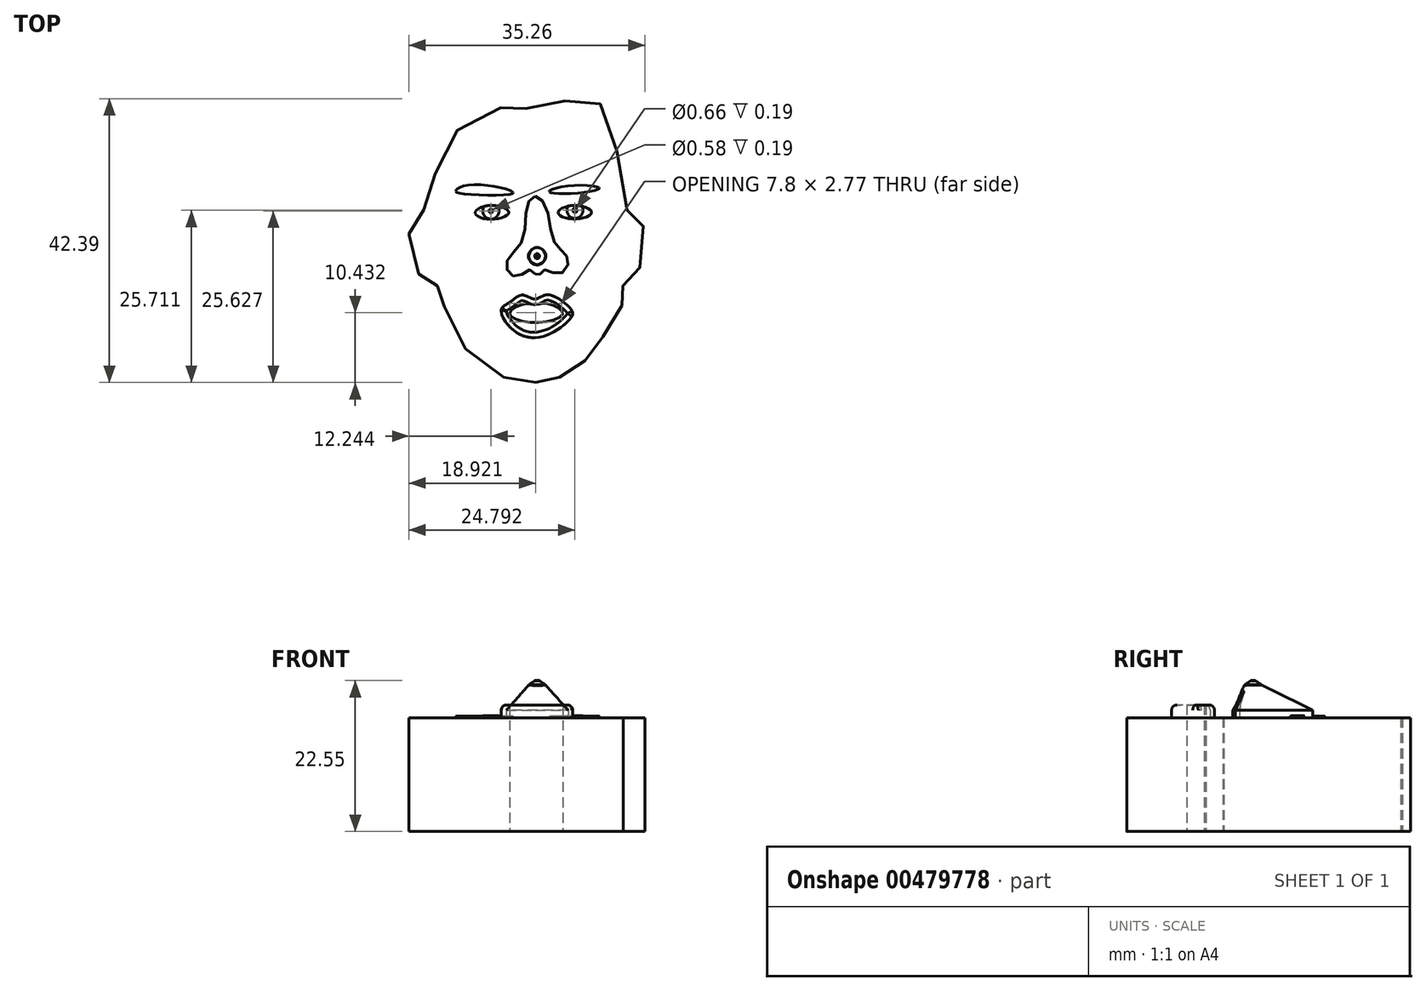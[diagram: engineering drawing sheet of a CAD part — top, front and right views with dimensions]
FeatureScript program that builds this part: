
annotation { "Feature Type Name" : "Feature", "Feature Type Description" : "" }
export const myFeature = defineFeature(function(context is Context, id is Id, definition is map)
    precondition{}
    {
        {
            var Q0;
            Q0=qCreatedBy(makeId("Top.planeOp"),FACE);
            var sketch = newSketch(context, id + "F0", { "sketchPlane" : qUnion([Q0])});
            skFitSpline(sketch, "E0", {"points": [v(0.4, -22.75) * mm, v(-4.87, -21.75) * mm, v(-12.74, -13.42) * mm, v(-13.89, -8.3) * mm, v(-14.73, -8.38) * mm, v(-17.1, -6.47) * mm, v(-18.24, 0.86) * mm, v(-15.72, 3.84) * mm, v(-12.97, 13.09) * mm, v(-3.8, 18.44) * mm, v(-1.2, 18.14) * mm, v(6.52, 19.59) * mm, v(11.26, 17.14) * mm, v(14.54, 1.94) * mm, v(16.3, 0.95) * mm, v(15.46, -6.54) * mm, v(13.47, -8.22) * mm, v(13.43, -8.87) * mm, v(13.1, -11.77) * mm, v(9.22, -17.47) * mm, v(7.15, -20.1) * mm, v(2.92, -22.33) * mm, v(0.4, -22.75) * mm]});
            skFitSpline(sketch, "E1", {"points": [v(-11.56, 5.85) * mm, v(-10.22, 6.65) * mm, v(-4.5, 6.26) * mm, v(-3, 5.51) * mm, v(-10, 5.38) * mm, v(-11.56, 5.85) * mm]});
            skFitSpline(sketch, "E2", {"points": [v(2.41, 5.72) * mm, v(5.43, 6.65) * mm, v(9.9, 6.3) * mm, v(6.97, 5.59) * mm, v(2.41, 5.72) * mm]});
            skFitSpline(sketch, "E3", {"points": [v(3.74, 2.65) * mm, v(6, 1.68) * mm, v(8.72, 2.63) * mm, v(6.32, 3.72) * mm, v(3.74, 2.65) * mm]});
            skCircle(sketch, "E4", {"center": v(6.25, 2.96) * mm, "radius": 0.33 * mm});
            skArc(sketch, "E5", {"start": v(5.24, 3.6) * mm, "mid": v(6.25, 1.76) * mm, "end": v(7.27, 3.6) * mm});
            skFitSpline(sketch, "E6", {"points": [v(-8.65, 2.59) * mm, v(-6.37, 3.7) * mm, v(-3.61, 2.65) * mm, v(-6.23, 1.61) * mm, v(-8.65, 2.59) * mm]});
            skCircle(sketch, "E7", {"center": v(-6.3, 2.88) * mm, "radius": 0.3 * mm});
            skArc(sketch, "E8", {"start": v(-7.3, 3.56) * mm, "mid": v(-6.26, 1.66) * mm, "end": v(-5.33, 3.62) * mm});
            skFitSpline(sketch, "E9", {"points": [v(-4.77, -11.97) * mm, v(-3.44, -10.74) * mm, v(-1.6, -9.67) * mm, v(0.29, -10.29) * mm, v(2.2, -9.64) * mm, v(5.8, -12.04) * mm, v(5.69, -13.03) * mm, v(3.08, -15.2) * mm, v(-1.88, -15.61) * mm, v(-4.77, -11.97) * mm]});
            skFitSpline(sketch, "E10", {"points": [v(-3.52, -12.43) * mm, v(-1.17, -11) * mm, v(0.27, -11.15) * mm, v(1.78, -10.9) * mm, v(4.43, -12.34) * mm, v(0.56, -13.8) * mm, v(-3.52, -12.43) * mm]});
            skFitSpline(sketch, "E11", {"points": [v(0.34, 5.06) * mm, v(1.94, 3.41) * mm, v(3.16, -1.8) * mm, v(4.65, -3.4) * mm, v(5.24, -5.08) * mm, v(3.78, -6.54) * mm, v(1.74, -5.91) * mm, v(0.98, -6.62) * mm, v(0.49, -6.67) * mm, v(-0.4, -5.91) * mm, v(-2.12, -6.85) * mm, v(-3.77, -6.2) * mm, v(-3.69, -4.22) * mm, v(-1.63, -1.63) * mm, v(-0.9, 3.56) * mm, v(0.34, 5.06) * mm]});
            skSolve(sketch);
        }
        {
            var Q0;
            Q0=makeQuery(id+"F0.imprint","IMPRINT",FACE,{"disambiguationData":[TD([[makeQuery(id+"F0.imprint","IMPRINT",EDGE,{"derivedFrom":sQuery(id+"F0.wireOp",EDGE,"E0")}),-1.0]])]});
            extrude(context, id + "F1", {"entities" : qUnion([Q0]), "depth" : 17 * mm});
        }
        {
            var Q0;
            Q0=makeQuery(id+"F0.imprint","IMPRINT",FACE,{"disambiguationData":[TD([[makeQuery(id+"F0.imprint","IMPRINT",EDGE,{"derivedFrom":sQuery(id+"F0.wireOp",EDGE,"E11")}),-1.0]])]});
            extrude(context, id + "F2", {"entities" : qUnion([Q0]), "operationType" : NewBodyOperationType.ADD, "depth" : 18.1 * mm});
        }
        {
            var Q0;
            Q0=makeQuery(id+"F0.imprint","IMPRINT",FACE,{"disambiguationData":[TD([[makeQuery(id+"F0.imprint","IMPRINT",EDGE,{"derivedFrom":sQuery(id+"F0.wireOp",EDGE,"E2")}),-1.0]])]});
            var Q1;
            Q1=makeQuery(id+"F0.imprint","IMPRINT",FACE,{"disambiguationData":[TD([[makeQuery(id+"F0.imprint","IMPRINT",EDGE,{"derivedFrom":sQuery(id+"F0.wireOp",EDGE,"E1")}),-1.0]])]});
            extrude(context, id + "F3", {"entities" : qUnion([Q0, Q1]), "operationType" : NewBodyOperationType.ADD, "depth" : 17.2 * mm});
        }
        {
            var Q0;
            {var subQ0=sQuery(id+"F0.wireOp",EDGE,"E8");Q0=makeQuery(id+"F0.imprint","IMPRINT",FACE,{"disambiguationData":[TD([[makeQuery(id+"F0.imprint","IMPRINT",EDGE,{"derivedFrom":subQ0}),-1.0]])]});}
            var Q1;
            {var subQ0=sQuery(id+"F0.wireOp",EDGE,"E5");Q1=makeQuery(id+"F0.imprint","IMPRINT",FACE,{"disambiguationData":[TD([[makeQuery(id+"F0.imprint","IMPRINT",EDGE,{"derivedFrom":subQ0}),-1.0]])]});}
            extrude(context, id + "F4", {"entities" : qUnion([Q0, Q1]), "operationType" : NewBodyOperationType.ADD, "depth" : 17.2 * mm});
        }
        {
            var Q0;
            Q0=makeQuery(id+"F0.imprint","IMPRINT",FACE,{"disambiguationData":[TD([[makeQuery(id+"F0.imprint","IMPRINT",EDGE,{"derivedFrom":sQuery(id+"F0.wireOp",EDGE,"E7")}),-1.0]])]});
            var Q1;
            Q1=makeQuery(id+"F0.imprint","IMPRINT",FACE,{"disambiguationData":[TD([[makeQuery(id+"F0.imprint","IMPRINT",EDGE,{"derivedFrom":sQuery(id+"F0.wireOp",EDGE,"E4")}),-1.0]])]});
            extrude(context, id + "F5", {"entities" : qUnion([Q0, Q1]), "operationType" : NewBodyOperationType.ADD, "depth" : 17.32 * mm});
        }
        {
            var Q0;
            Q0=makeQuery(id+"F0.imprint","IMPRINT",FACE,{"disambiguationData":[TD([[makeQuery(id+"F0.imprint","IMPRINT",EDGE,{"derivedFrom":sQuery(id+"F0.wireOp",EDGE,"E4")}),1.0]])]});
            var Q1;
            Q1=makeQuery(id+"F0.imprint","IMPRINT",FACE,{"disambiguationData":[TD([[makeQuery(id+"F0.imprint","IMPRINT",EDGE,{"derivedFrom":sQuery(id+"F0.wireOp",EDGE,"E7")}),1.0]])]});
            extrude(context, id + "F6", {"entities" : qUnion([Q0, Q1]), "operationType" : NewBodyOperationType.ADD, "depth" : 17.13 * mm});
        }
        {
            var Q0;
            Q0=makeQuery(id+"F0.imprint","IMPRINT",FACE,{"disambiguationData":[TD([[makeQuery(id+"F0.imprint","IMPRINT",EDGE,{"derivedFrom":sQuery(id+"F0.wireOp",EDGE,"E9")}),-1.0]])]});
            extrude(context, id + "F7", {"entities" : qUnion([Q0]), "operationType" : NewBodyOperationType.ADD, "depth" : 18.9 * mm});
        }
        {
            var Q0;
            Q0=makeQuery(id+"F7.opExtrude","CAP_EDGE",EDGE,{"disambiguationData":[OSD([sQuery(id+"F0.wireOp",EDGE,"E9")])],"isStart":false});
            fillet(context, id + "F8", {"entities" : qUnion([Q0]), "radius" : 0.8 * mm, "tangentPropagation" : true, "allowEdgeOverflow" : false});
        }
        {
            var Q0;
            Q0=makeQuery(id+"F2.opExtrude","CAP_FACE",FACE,{"disambiguationData":[OSD([sQuery(id+"F0.wireOp",EDGE,"E11")])],"isStart":false});
            cPlane(context, id + "F9", {"entities" : qUnion([Q0]), "cplaneType" : CPlaneType.OFFSET, "offset" : 3.78 * mm, "width" : 150 * mm, "height" : 150 * mm});
        }
        {
            var Q0;
            Q0=qCreatedBy(id+"F9.planeOp",FACE);
            var sketch = newSketch(context, id + "F10", { "sketchPlane" : qUnion([Q0])});
            skFitSpline(sketch, "E12", {"points": [v(0.6, -5.19) * mm, v(-0.68, -3.87) * mm, v(0.56, -2.58) * mm, v(1.88, -3.83) * mm, v(0.6, -5.19) * mm]});
            skSolve(sketch);
        }
        {
            var Q0;
            Q0=makeQuery(id+"F2.opExtrude","CAP_FACE",FACE,{"disambiguationData":[OSD([sQuery(id+"F0.wireOp",EDGE,"E11")])],"isStart":false});
            var Q1;
            Q1=makeQuery(id+"F10.imprint","IMPRINT",FACE,{"disambiguationData":[TD([[makeQuery(id+"F10.imprint","IMPRINT",EDGE,{"derivedFrom":sQuery(id+"F10.wireOp",EDGE,"E12")}),-1.0]])]});
            loft(context, id + "F11", {"sheetProfilesArray" : [{ "sheetProfileEntities" : qUnion([Q0]) }, { "sheetProfileEntities" : qUnion([Q1]) }]});
        }
        {
            var Q0;
            Q0=makeQuery(id+"F11.opLoft","CAP_FACE",FACE,{"disambiguationData":[OSD([makeQuery(id+"F10.imprint","IMPRINT",FACE,{"disambiguationData":[TD([[makeQuery(id+"F10.imprint","IMPRINT",EDGE,{"derivedFrom":sQuery(id+"F10.wireOp",EDGE,"E12")}),-1.0]])]})])],"isStart":true});
            cPlane(context, id + "F12", {"entities" : qUnion([Q0]), "cplaneType" : CPlaneType.OFFSET, "offset" : 0.67 * mm, "width" : 150 * mm, "height" : 150 * mm});
        }
        {
            var Q0;
            Q0=qCreatedBy(id+"F12.planeOp",FACE);
            var sketch = newSketch(context, id + "F13", { "sketchPlane" : qUnion([Q0])});
            skCircle(sketch, "E13", {"center": v(0.6, -3.87) * mm, "radius": 0.3 * mm});
            skSolve(sketch);
        }
        {
            var Q1;
            Q1=makeQuery(id+"F11.opLoft","CAP_FACE",FACE,{"disambiguationData":[OSD([makeQuery(id+"F10.imprint","IMPRINT",FACE,{"disambiguationData":[TD([[makeQuery(id+"F10.imprint","IMPRINT",EDGE,{"derivedFrom":sQuery(id+"F10.wireOp",EDGE,"E12")}),-1.0]])]})])],"isStart":true});
            var Q2;
            Q2=makeQuery(id+"F13.imprint","IMPRINT",FACE,{"disambiguationData":[TD([[makeQuery(id+"F13.imprint","IMPRINT",EDGE,{"derivedFrom":sQuery(id+"F13.wireOp",EDGE,"E13")}),1.0]])]});
            loft(context, id + "F14", {"operationType" : NewBodyOperationType.ADD, "sheetProfilesArray" : [{ "sheetProfileEntities" : qUnion([Q1]) }, { "sheetProfileEntities" : qUnion([Q2]) }]});
        }
        {
            var Q0;
            {var subQ0=sQuery(id+"F10.wireOp",EDGE,"E12");var subQ1=sQuery(id+"F0.wireOp",EDGE,"E11");Q0=makeQuery(id+"F14.boolean.opBoolean","MERGE",EDGE,{"derivedFrom":[makeQuery(id+"F11.opLoft","MID_CAP_EDGE",EDGE,{"disambiguationData":[OSD([subQ1,subQ0])],"capPos":1.0}),makeQuery(id+"F14.opLoft","MID_CAP_EDGE",EDGE,{"disambiguationData":[OSD([subQ1,subQ0])],"capPos":0.0})]});}
            fillet(context, id + "F15", {"entities" : qUnion([Q0]), "radius" : 0.22 * mm, "tangentPropagation" : true, "allowEdgeOverflow" : false});
        }
        {
            var Q0;
            Q0=makeQuery(id+"F14.opLoft","MID_CAP_EDGE",EDGE,{"disambiguationData":[OSD([sQuery(id+"F0.wireOp",EDGE,"E11"),sQuery(id+"F10.wireOp",EDGE,"E12"),sQuery(id+"F13.wireOp",EDGE,"E13")])],"capPos":1.0});
            fillet(context, id + "F16", {"entities" : qUnion([Q0]), "radius" : 0.2 * mm, "tangentPropagation" : true, "allowEdgeOverflow" : false});
        }
    });
